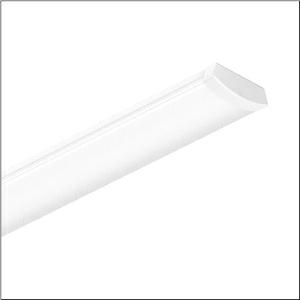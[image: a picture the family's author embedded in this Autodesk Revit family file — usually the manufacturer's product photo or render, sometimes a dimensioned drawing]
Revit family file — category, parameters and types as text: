
# Revit family: siluette_21_51ln12mnm70a
name_source: partatom
category: Lighting Fixtures
units: mm (PartAtom-declared; Revit-internal decimal feet)

## family parameters
Cut with Voids When Loaded = No
Host = Face
Light Source = No
Part Type = Normal
Room Calculation Point = No
Round Connector Dimension = Use Diameter
Shared = No

## types (1)
- --- (1 x LED, 4320 lm, 28.8 W, 5000K)
    Apparent Load = 29 VA
    CIE Flux Codes = 43 73 92 94 100
    Color Rendering = 80
    Color Temperature = 5000K
    Default Elevation = 1800 mm
    Description = Siluette 21, office luminaire, primary optical cover: enclosure, of PC, frosted, light emission: direct distribution, primary light characteristic: symmetric, installation type: suspended mounting, surface-mounted, LED, rated luminous flux: 7.150lm, luminous efficacy: 147lm/W, light colour: 830/840/850, colour temperature: 3000/4000/5000K, control gear: ON/OFF Multilumen, with terminal, 3-pole, mains connection: 220..240V, AC, 50/60Hz, rated input power: 49W, housing, of sheet steel, white, length: 1.500mm, width: 152mm, height: 53mm, end cap, of PMMA, white, protection rating (complete): IP44, insulation class (complete): insulation class I (protective earthing), certification: CE, UKCA, protection symbol: D, impact resistance: IK04, permissible operating ambient temperature: -20..+40°C, contact your sales advisor before using the luminaires in applications with unclear chemical exposure, large temperature fluctuations or condensation-forming humidity, corresponds to IFS (International Featured Standards) requirements for safety and quality in the food industry, packaging unit: 1 piece
    Height = 52 mm  [stored 0.170604 ft]
    Lamp = 1 x LED
    Lamp Light Flux = 4320 lm
    Lamp Power = 28.8 W
    Lamp count = 1
    Length = 1485 mm
    Luminous efficacy = 150 lm/W
    Manufacturer = Siteco
    ModVariant = No
    Model = 51LN12MNM70A
    Mounting Place = Ceiling
    Mounting Type = Pendant
    Number of Poles = 1
    OnlyDefault = Yes
    Power Factor = 1
    Product Name = Siluette 21
    Product group = office luminaire | ceiling pendant
    ProductGroupID = 903
    Protection Class = Protection class I
    Protection Degree = IP 44
    RLX_Detail_Level = 1
    RLX_Emergency_Light_Flux = 0 lm
    RLX_Emergency_Type = 0
    RLX_Emergency_Type_DB = No
    RlxData = <blob elided: 19189 chars, md5=9f21a18e>
    Socket = socket
    Standby Power = 0 W
    System Light Flux = 4320 lm
    System Power = 29 W
    Type Comments = individual setting: colour temperature 5000K, luminous flux: 61 % | (OFF | OFF | ON) | 200 mA
    Type Image = l_1296910.jpg
    URL = http://relux.com
    VarID = @adj_067359
    Voltage = 0 V
    Weight = 0.00 kg
    Width = 152 mm

note: [stored X ft] marks values corroborated as IEEE doubles in the binary element streams (Revit-internal decimal feet)

## geometry (parser evidence)
native form markers: Blend x4, Sweep x12
no freeform markers — native parametric forms only
